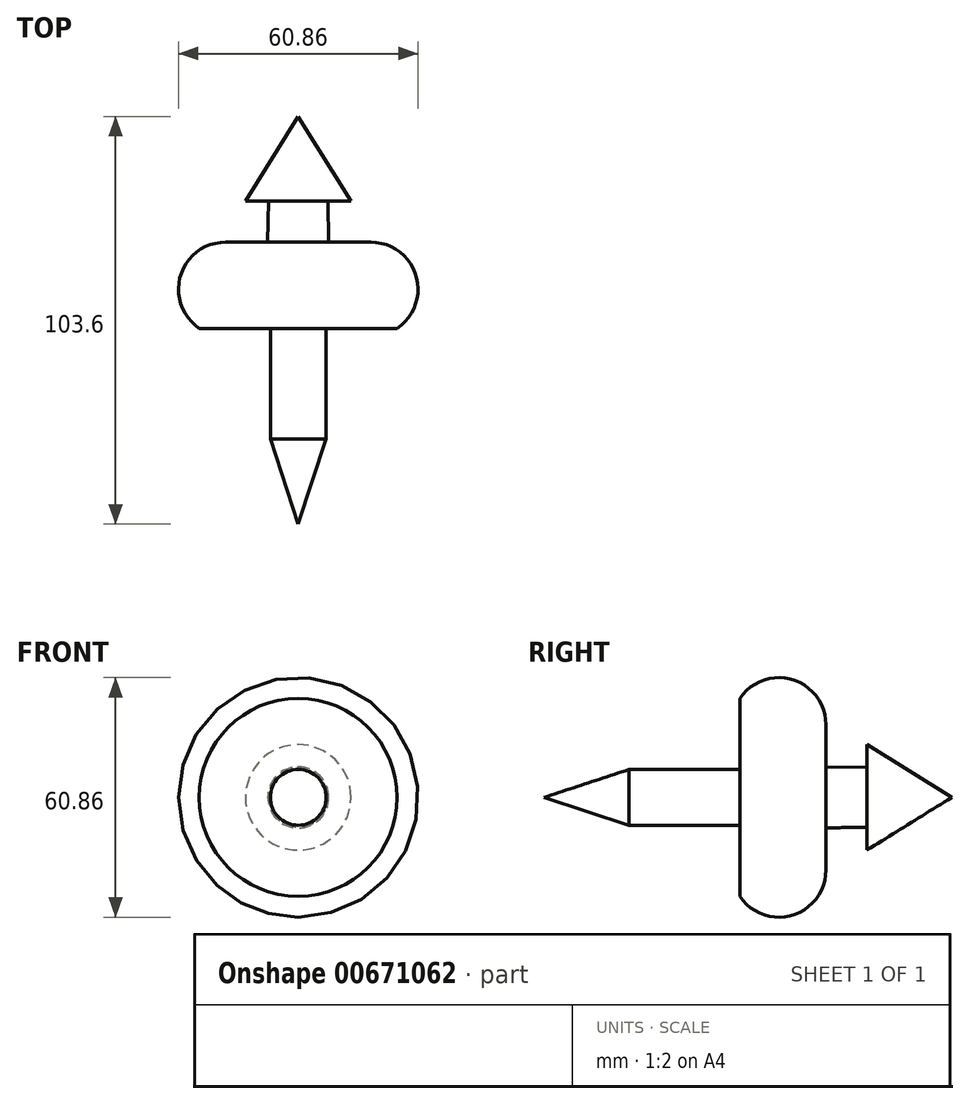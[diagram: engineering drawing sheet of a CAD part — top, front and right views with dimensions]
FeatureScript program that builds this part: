
annotation { "Feature Type Name" : "Feature", "Feature Type Description" : "" }
export const myFeature = defineFeature(function(context is Context, id is Id, definition is map)
    precondition{}
    {
        {
            var Q0;
            Q0=qCreatedBy(makeId("Right.planeOp"),FACE);
            var sketch = newSketch(context, id + "F0", { "sketchPlane" : qUnion([Q0])});
            skLineSegment(sketch, "E0", {"start": v(-26.81, 0) * mm, "end": v(-26.81, 25.15) * mm});
            skLineSegment(sketch, "E1", {"start": v(-26.81, 0) * mm, "end": v(0, 0) * mm});
            skLineSegment(sketch, "E2", {"start": v(0, 0) * mm, "end": v(27.04, 0) * mm});
            skLineSegment(sketch, "E3", {"start": v(27.04, 0) * mm, "end": v(5.5, 13.4) * mm});
            skLineSegment(sketch, "E4", {"start": v(5.5, 13.4) * mm, "end": v(5.5, 7.58) * mm});
            skLineSegment(sketch, "E5", {"start": v(5.5, 7.58) * mm, "end": v(-4.93, 7.75) * mm});
            skLineSegment(sketch, "E6", {"start": v(-4.93, 7.75) * mm, "end": v(-4.93, 18.47) * mm});
            skArc(sketch, "E7", {"start": v(-4.93, 18.47) * mm, "mid": v(-13.4, 29.91) * mm, "end": v(-26.81, 25.15) * mm});
            skSolve(sketch);
        }
        {
            var Q0;
            Q0 = qSketchRegion(id + "F0", true);
            var Q1;
            Q1=sQuery(id+"F0.wireOp",EDGE,"E1");
            revolve(context, id + "F1", {"entities" : qUnion([Q0]), "axis" : qUnion([Q1]), "revolveType" : RevolveType.FULL});
        }
        {
            var Q0;
            Q0=qCreatedBy(makeId("Right.planeOp"),FACE);
            var sketch = newSketch(context, id + "F2", { "sketchPlane" : qUnion([Q0])});
            skLineSegment(sketch, "E8.bottom", {"start": v(-54.94, 7.09) * mm, "end": v(0, 7.09) * mm});
            skLineSegment(sketch, "E8.top", {"start": v(-54.94, 0) * mm, "end": v(0, 0) * mm});
            skLineSegment(sketch, "E8.left", {"start": v(-54.94, 7.09) * mm, "end": v(-54.94, 0) * mm});
            skLineSegment(sketch, "E8.right", {"start": v(0, 7.09) * mm, "end": v(0, 0) * mm});
            skLineSegment(sketch, "E9", {"start": v(-76.56, 0) * mm, "end": v(-54.94, 7.09) * mm});
            skLineSegment(sketch, "E10", {"start": v(-76.56, 0) * mm, "end": v(-54.94, 0) * mm});
            skSolve(sketch);
        }
        {
            var Q0;
            Q0 = qSketchRegion(id + "F2", true);
            var Q1;
            Q1=sQuery(id+"F2.wireOp",EDGE,"E8.top");
            revolve(context, id + "F3", {"operationType" : NewBodyOperationType.ADD, "entities" : qUnion([Q0]), "axis" : qUnion([Q1]), "revolveType" : RevolveType.FULL});
        }
    });
